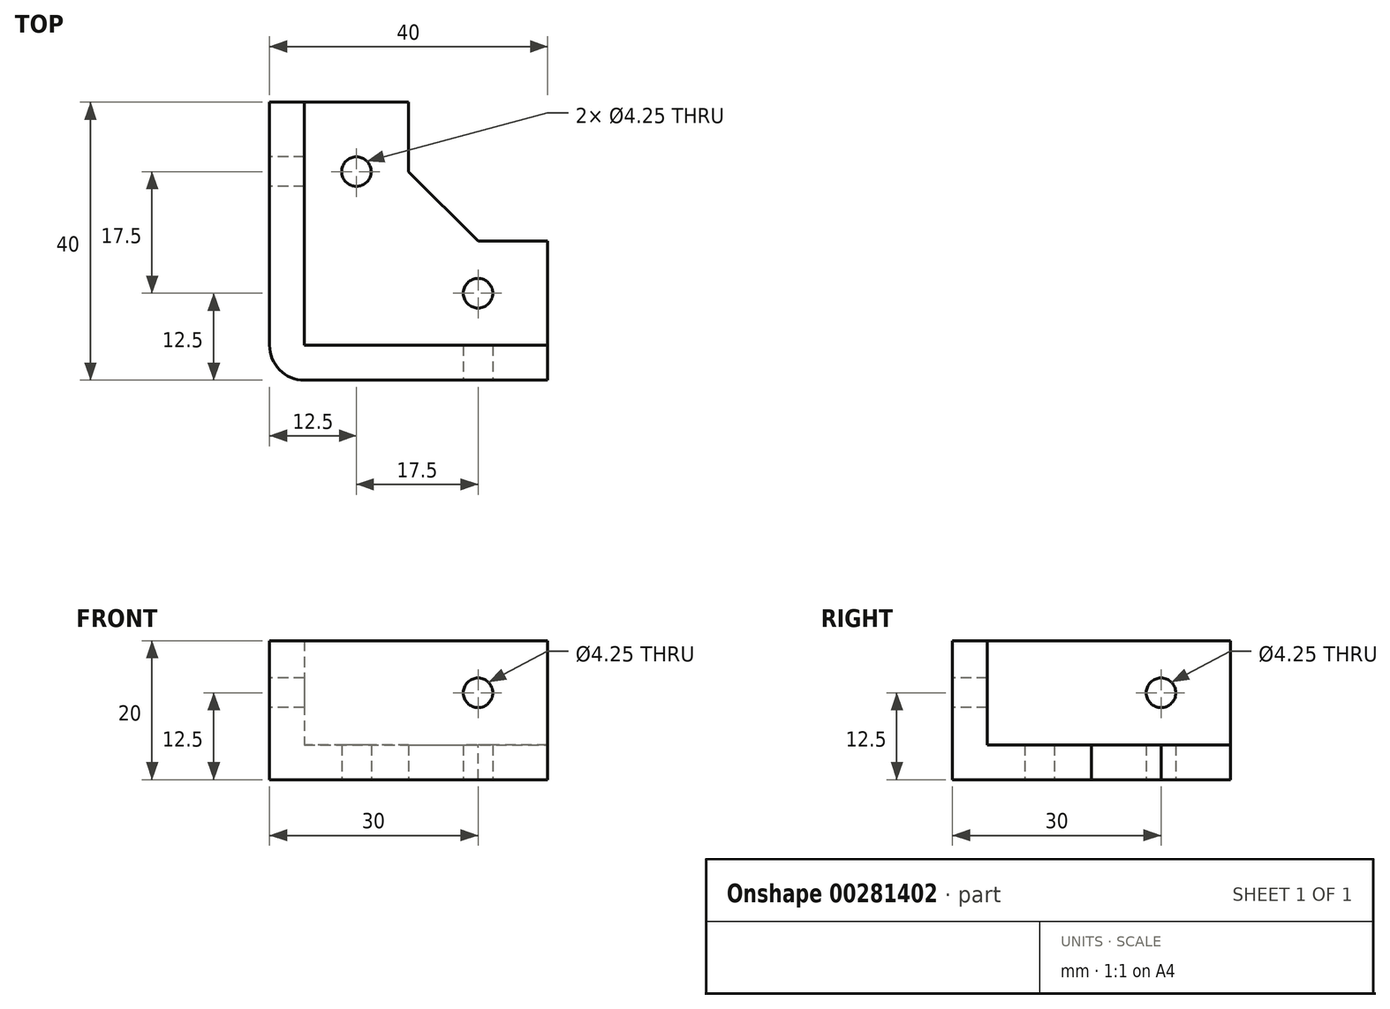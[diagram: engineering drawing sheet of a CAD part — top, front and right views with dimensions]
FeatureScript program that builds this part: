
annotation { "Feature Type Name" : "Feature", "Feature Type Description" : "" }
export const myFeature = defineFeature(function(context is Context, id is Id, definition is map)
    precondition{}
    {
        {
            var Q0;
            Q0=qCreatedBy(makeId("Top.planeOp"),FACE);
            var sketch = newSketch(context, id + "F0", { "sketchPlane" : qUnion([Q0])});
            skLineSegment(sketch, "E0", {"start": v(0, 40) * mm, "end": v(-20, 40) * mm});
            skLineSegment(sketch, "E1", {"start": v(-20, 40) * mm, "end": v(-20, 0) * mm});
            skLineSegment(sketch, "E2", {"start": v(-20, 0) * mm, "end": v(20, 0) * mm});
            skLineSegment(sketch, "E3", {"start": v(20, 0) * mm, "end": v(20, 20) * mm});
            skLineSegment(sketch, "E4", {"start": v(20, 20) * mm, "end": v(0, 20) * mm});
            skLineSegment(sketch, "E5", {"start": v(0, 20) * mm, "end": v(0, 40) * mm});
            skCircle(sketch, "E6", {"center": v(-7.5, 30) * mm, "radius": 2.12 * mm});
            skCircle(sketch, "E7", {"center": v(10, 12.5) * mm, "radius": 2.12 * mm});
            skCircle(sketch, "E8", {"center": v(-7.5, 12.5) * mm, "radius": 2.12 * mm, "construction": true});
            skSolve(sketch);
        }
        {
            var Q0;
            Q0=qSketchRegion(id+"F0",true);
            extrude(context, id + "F1", {"entities" : qUnion([Q0]), "depth" : 5 * mm});
        }
        {
            var Q0;
            Q0=makeQuery(id+"F1.opExtrude","CAP_FACE",FACE,{"disambiguationData":[OSD([sQuery(id+"F0.wireOp",EDGE,"E0"),sQuery(id+"F0.wireOp",EDGE,"E1"),sQuery(id+"F0.wireOp",EDGE,"E2"),sQuery(id+"F0.wireOp",EDGE,"E3"),sQuery(id+"F0.wireOp",EDGE,"E4"),sQuery(id+"F0.wireOp",EDGE,"E5"),sQuery(id+"F0.wireOp",EDGE,"E6"),sQuery(id+"F0.wireOp",EDGE,"E7")])],"isStart":false});
            var sketch = newSketch(context, id + "F2", { "sketchPlane" : qUnion([Q0])});
            skLineSegment(sketch, "E9", {"start": v(-20, 40) * mm, "end": v(-15, 40) * mm});
            skLineSegment(sketch, "E10", {"start": v(-15, 40) * mm, "end": v(-15, 5) * mm});
            skLineSegment(sketch, "E11", {"start": v(-15, 5) * mm, "end": v(20, 5) * mm});
            skLineSegment(sketch, "E12", {"start": v(20, 5) * mm, "end": v(20, 0) * mm});
            skLineSegment(sketch, "E13", {"start": v(20, 0) * mm, "end": v(-20, 0) * mm});
            skLineSegment(sketch, "E14", {"start": v(-20, 0) * mm, "end": v(-20, 40) * mm});
            skSolve(sketch);
        }
        {
            var Q0;
            Q0=qSketchRegion(id+"F2",true);
            extrude(context, id + "F3", {"entities" : qUnion([Q0]), "operationType" : NewBodyOperationType.ADD, "depth" : 15 * mm});
        }
        {
            var Q0;
            Q0=makeQuery(id+"F1.opExtrude","SWEPT_EDGE",EDGE,{"disambiguationData":[OSD([sQuery(id+"F0.wireOp",EDGE,"E4"),sQuery(id+"F0.wireOp",EDGE,"E5")])]});
            var Q1;
            Q1=makeQuery(id+"F76PTgu7nN6sp4q_1.opExtrude","CAP_EDGE",EDGE,{"disambiguationData":[OSD([sQuery(id+"FVZp2BhR3DRSIo4_1.wireOp",EDGE,"NxikKBTB-JvOB-kXal-Y067-Dro2nPYKC55K")])],"isStart":true});
            var Q2;
            Q2=makeQuery(id+"F76PTgu7nN6sp4q_1.opExtrude","CAP_EDGE",EDGE,{"disambiguationData":[OSD([sQuery(id+"FVZp2BhR3DRSIo4_1.wireOp",EDGE,"2QbokhEA-Neii-4Odm-KCon-wAkmbLHXTRdn")])],"isStart":true});
            chamfer(context, id + "F4", {"entities" : qUnion([Q0, Q1, Q2]), "width" : 10 * mm, "tangentPropagation" : true});
        }
        {
            var Q0;
            Q0=makeQuery(id+"F76PTgu7nN6sp4q_1.boolean.opBoolean","MERGE",FACE,{"derivedFrom":[makeQuery(id+"F3.boolean.opBoolean","MERGE",FACE,{"derivedFrom":[makeQuery(id+"F1.opExtrude","SWEPT_FACE",FACE,{"disambiguationData":[OSD([sQuery(id+"F0.wireOp",EDGE,"E2")])]}),makeQuery(id+"F3.opExtrude","SWEPT_FACE",FACE,{"disambiguationData":[OSD([sQuery(id+"F2.wireOp",EDGE,"E13")])]})]}),makeQuery(id+"F76PTgu7nN6sp4q_1.opExtrude","SWEPT_FACE",FACE,{"disambiguationData":[OSD([sQuery(id+"FVZp2BhR3DRSIo4_1.wireOp",EDGE,"PXxosK55-A00r-EiAo-lVqn-v3T7ZulwWpec")])]})]});
            var sketch = newSketch(context, id + "F5", { "sketchPlane" : qUnion([Q0])});
            skCircle(sketch, "E15", {"center": v(10, 12.5) * mm, "radius": 2.12 * mm});
            skSolve(sketch);
        }
        {
            var Q0;
            Q0=qSketchRegion(id+"F5",true);
            extrude(context, id + "F6", {"entities" : qUnion([Q0]), "operationType" : NewBodyOperationType.REMOVE, "oppositeDirection" : true, "depth" : 5 * mm});
        }
        {
            var Q0;
            Q0=makeQuery(id+"F76PTgu7nN6sp4q_1.boolean.opBoolean","MERGE",FACE,{"derivedFrom":[makeQuery(id+"F3.boolean.opBoolean","MERGE",FACE,{"derivedFrom":[makeQuery(id+"F1.opExtrude","SWEPT_FACE",FACE,{"disambiguationData":[OSD([sQuery(id+"F0.wireOp",EDGE,"E1")])]}),makeQuery(id+"F3.opExtrude","SWEPT_FACE",FACE,{"disambiguationData":[OSD([sQuery(id+"F2.wireOp",EDGE,"E14")])]})]}),makeQuery(id+"F76PTgu7nN6sp4q_1.opExtrude","SWEPT_FACE",FACE,{"disambiguationData":[OSD([sQuery(id+"FVZp2BhR3DRSIo4_1.wireOp",EDGE,"IHTPssIf-bVww-9Vql-ndyx-yP6tfeN2iFFo")])]})]});
            var sketch = newSketch(context, id + "F7", { "sketchPlane" : qUnion([Q0])});
            skCircle(sketch, "E16", {"center": v(-30, 12.5) * mm, "radius": 2.12 * mm});
            skSolve(sketch);
        }
        {
            var Q0;
            Q0=qSketchRegion(id+"F7",true);
            extrude(context, id + "F8", {"entities" : qUnion([Q0]), "operationType" : NewBodyOperationType.REMOVE, "oppositeDirection" : true, "depth" : 5 * mm});
        }
        {
            var Q0;
            Q0=makeQuery(id+"F76PTgu7nN6sp4q_1.boolean.opBoolean","MERGE",EDGE,{"derivedFrom":[makeQuery(id+"F3.boolean.opBoolean","MERGE",EDGE,{"derivedFrom":[makeQuery(id+"F1.opExtrude","SWEPT_EDGE",EDGE,{"disambiguationData":[OSD([sQuery(id+"F0.wireOp",EDGE,"E1"),sQuery(id+"F0.wireOp",EDGE,"E2")])]}),makeQuery(id+"F3.opExtrude","SWEPT_EDGE",EDGE,{"disambiguationData":[OSD([sQuery(id+"F2.wireOp",EDGE,"E13"),sQuery(id+"F2.wireOp",EDGE,"E14")])]})]}),makeQuery(id+"F76PTgu7nN6sp4q_1.opExtrude","SWEPT_EDGE",EDGE,{"disambiguationData":[OSD([sQuery(id+"FVZp2BhR3DRSIo4_1.wireOp",EDGE,"IHTPssIf-bVww-9Vql-ndyx-yP6tfeN2iFFo"),sQuery(id+"FVZp2BhR3DRSIo4_1.wireOp",EDGE,"PXxosK55-A00r-EiAo-lVqn-v3T7ZulwWpec")])]})]});
            fillet(context, id + "F9", {"entities" : qUnion([Q0]), "radius" : 5 * mm, "tangentPropagation" : true, "allowEdgeOverflow" : false});
        }
    });
